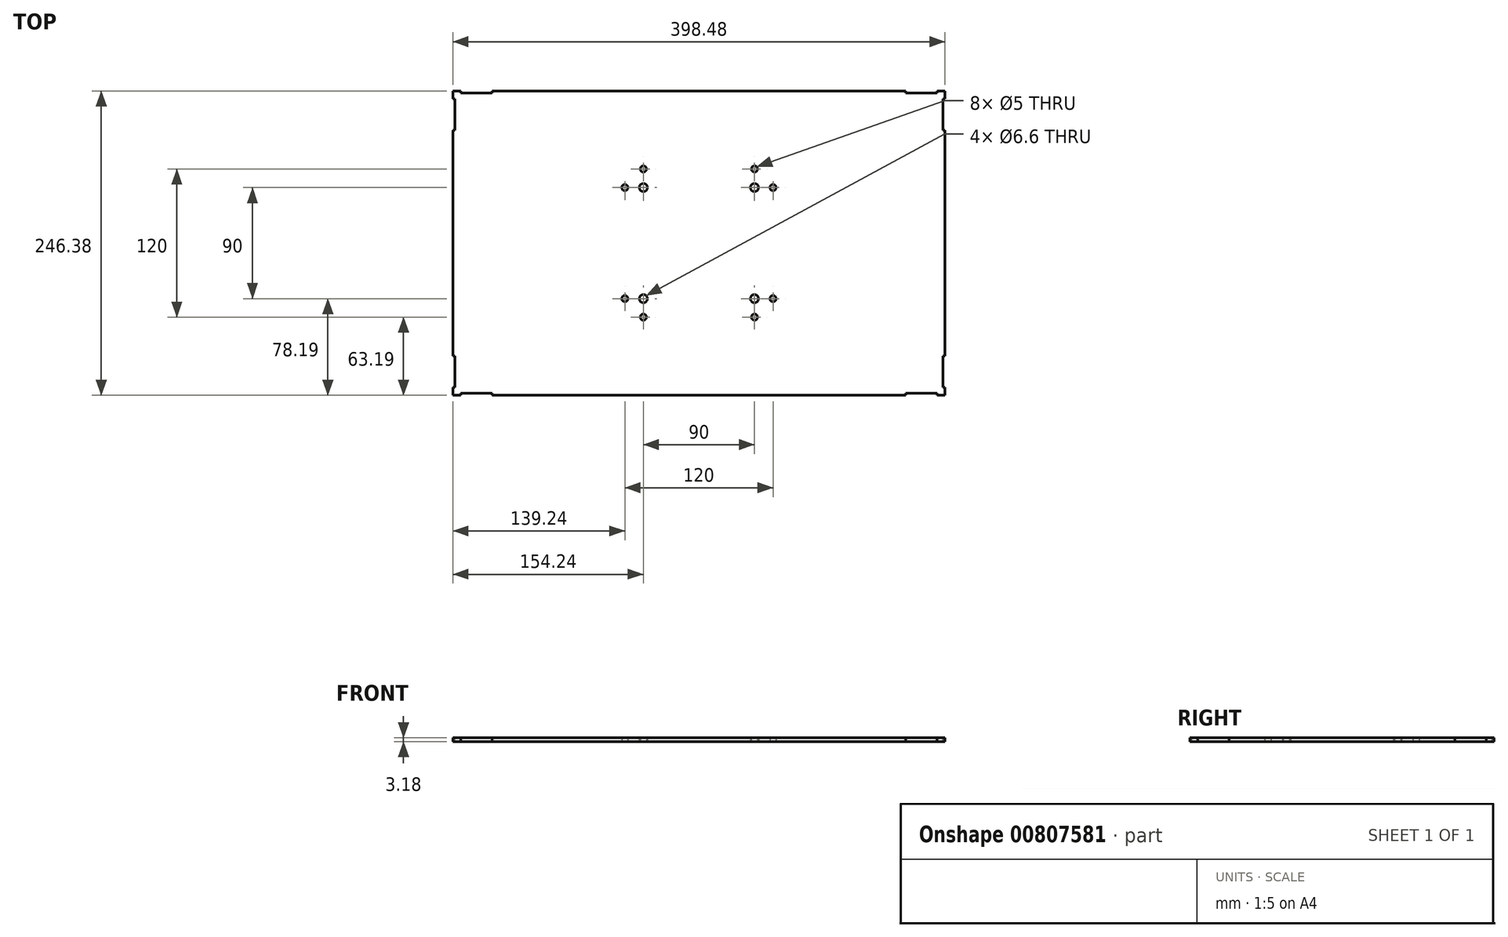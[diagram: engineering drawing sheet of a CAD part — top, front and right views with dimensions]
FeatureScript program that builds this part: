
annotation { "Feature Type Name" : "Feature", "Feature Type Description" : "" }
export const myFeature = defineFeature(function(context is Context, id is Id, definition is map)
    precondition{}
    {
        {
            var Q0;
            Q0=qCreatedBy(makeId("Top.planeOp"),FACE);
            var sketch = newSketch(context, id + "F0", { "sketchPlane" : qUnion([Q0])});
            skLineSegment(sketch, "E0.bottom", {"start": v(-199.24, 123.19) * mm, "end": v(199.24, 123.19) * mm});
            skLineSegment(sketch, "E0.top", {"start": v(-199.24, -123.2) * mm, "end": v(199.24, -123.2) * mm});
            skLineSegment(sketch, "E0.left", {"start": v(-199.24, 123.19) * mm, "end": v(-199.24, -123.2) * mm});
            skLineSegment(sketch, "E0.right", {"start": v(199.24, 123.19) * mm, "end": v(199.24, -123.19) * mm});
            skPoint(sketch, "E0.middle", {"position": v(0, 0) * mm});
            skLineSegment(sketch, "E1.bottom", {"start": v(45, 45) * mm, "end": v(-45, 45) * mm, "construction": true});
            skLineSegment(sketch, "E1.top", {"start": v(45, -45) * mm, "end": v(-45, -45) * mm, "construction": true});
            skLineSegment(sketch, "E1.left", {"start": v(45, 45) * mm, "end": v(45, -45) * mm, "construction": true});
            skLineSegment(sketch, "E1.right", {"start": v(-45, 45) * mm, "end": v(-45, -45) * mm, "construction": true});
            skCircle(sketch, "E2", {"center": v(-45, 45) * mm, "radius": 3.3 * mm});
            skCircle(sketch, "E3", {"center": v(45, 45) * mm, "radius": 3.3 * mm});
            skCircle(sketch, "E4", {"center": v(45, -45) * mm, "radius": 3.3 * mm});
            skCircle(sketch, "E5", {"center": v(-45, -45) * mm, "radius": 3.3 * mm});
            skCircle(sketch, "E6", {"center": v(-60, 45) * mm, "radius": 2.5 * mm});
            skCircle(sketch, "E7", {"center": v(-45, 60) * mm, "radius": 2.5 * mm});
            skCircle(sketch, "E8.MirrorC", {"center": v(45, 60) * mm, "radius": 2.5 * mm});
            skCircle(sketch, "E9.MirrorC", {"center": v(60, 45) * mm, "radius": 2.5 * mm});
            skCircle(sketch, "E10.MirrorC", {"center": v(45, -60) * mm, "radius": 2.5 * mm});
            skCircle(sketch, "E11.MirrorC", {"center": v(60, -45) * mm, "radius": 2.5 * mm});
            skCircle(sketch, "E12.MirrorC", {"center": v(-45, -60) * mm, "radius": 2.5 * mm});
            skCircle(sketch, "E13.MirrorC", {"center": v(-60, -45) * mm, "radius": 2.5 * mm});
            skSolve(sketch);
        }
        {
            var Q0;
            Q0=makeQuery(id+"F0.imprint","IMPRINT",FACE,{"disambiguationData":[TD([[makeQuery(id+"F0.imprint","IMPRINT",EDGE,{"derivedFrom":sQuery(id+"F0.wireOp",EDGE,"E0.bottom")}),-1.0]])]});
            extrude(context, id + "F1", {"entities" : qUnion([Q0]), "depth" : 3.17 * mm, "offsetDistance" : 25.4 * mm});
        }
        {
            var Q0;
            Q0=makeQuery(id+"F1.opExtrude","CAP_FACE",FACE,{"disambiguationData":[OSD([sQuery(id+"F0.wireOp",EDGE,"E0.bottom"),sQuery(id+"F0.wireOp",EDGE,"E0.top"),sQuery(id+"F0.wireOp",EDGE,"E0.left"),sQuery(id+"F0.wireOp",EDGE,"E0.right"),sQuery(id+"F0.wireOp",EDGE,"w9YSMrmx-gkuf-mAF0-RrVV-VzfJ2XjQqvrK.bottom"),sQuery(id+"F0.wireOp",EDGE,"w9YSMrmx-gkuf-mAF0-RrVV-VzfJ2XjQqvrK.top"),sQuery(id+"F0.wireOp",EDGE,"w9YSMrmx-gkuf-mAF0-RrVV-VzfJ2XjQqvrK.left"),sQuery(id+"F0.wireOp",EDGE,"w9YSMrmx-gkuf-mAF0-RrVV-VzfJ2XjQqvrK.right"),sQuery(id+"F0.wireOp",EDGE,"E2"),sQuery(id+"F0.wireOp",EDGE,"E3"),sQuery(id+"F0.wireOp",EDGE,"E4"),sQuery(id+"F0.wireOp",EDGE,"E5"),sQuery(id+"F0.wireOp",EDGE,"7fj2jC65-HHjj-RPa5-pwH1-fIjqxPNooKX1.bottom"),sQuery(id+"F0.wireOp",EDGE,"7fj2jC65-HHjj-RPa5-pwH1-fIjqxPNooKX1.top"),sQuery(id+"F0.wireOp",EDGE,"7fj2jC65-HHjj-RPa5-pwH1-fIjqxPNooKX1.right"),sQuery(id+"F0.wireOp",EDGE,"73IWlzh5-ptpZ-RGeC-0AsT-BQBUthGwBnOJ"),sQuery(id+"F0.wireOp",EDGE,"pzAkxvwE-vERC-Da5q-IG9L-KNYuP0dNzW4O"),sQuery(id+"F0.wireOp",EDGE,"hqBXGcnr-b5Qw-30Y7-EFE3-Enjm0PSFEsAV"),sQuery(id+"F0.wireOp",EDGE,"LVQ4rxL2-owo7-0TQt-NuUL-hCUhgpkdSAuj"),sQuery(id+"F0.wireOp",EDGE,"VEGctwco-K67i-BCNj-dZf2-I8q0qQZjCyYO"),sQuery(id+"F0.wireOp",EDGE,"W6IrgXfp-vklz-oZm7-d0sl-V1VckyniwT7Z")])],"isStart":false});
            var sketch = newSketch(context, id + "F2", { "sketchPlane" : qUnion([Q0])});
            skLineSegment(sketch, "E14.0", {"start": v(-199.24, 123.19) * mm, "end": v(199.24, 123.19) * mm, "construction": true});
            skLineSegment(sketch, "E14.1", {"start": v(-199.24, 123.19) * mm, "end": v(-199.24, -123.2) * mm, "construction": true});
            skLineSegment(sketch, "E14.2", {"start": v(-199.24, -123.2) * mm, "end": v(199.24, -123.2) * mm, "construction": true});
            skLineSegment(sketch, "E14.3", {"start": v(199.24, 123.19) * mm, "end": v(199.24, -123.2) * mm, "construction": true});
            skLineSegment(sketch, "E15.bottom", {"start": v(-192.89, 123.19) * mm, "end": v(-167.49, 123.19) * mm});
            skLineSegment(sketch, "E15.top", {"start": v(-192.89, 121.6) * mm, "end": v(-167.49, 121.6) * mm});
            skLineSegment(sketch, "E15.left", {"start": v(-192.89, 123.19) * mm, "end": v(-192.89, 121.6) * mm});
            skLineSegment(sketch, "E15.right", {"start": v(-167.49, 123.19) * mm, "end": v(-167.49, 121.6) * mm});
            skLineSegment(sketch, "E16.MirrorCS", {"start": v(192.89, 123.19) * mm, "end": v(192.89, 121.6) * mm});
            skLineSegment(sketch, "E17.MirrorCS", {"start": v(192.89, 121.6) * mm, "end": v(167.49, 121.6) * mm});
            skLineSegment(sketch, "E18.MirrorCS", {"start": v(167.49, 123.19) * mm, "end": v(167.49, 121.6) * mm});
            skLineSegment(sketch, "E19.MirrorCS", {"start": v(-192.89, -121.6) * mm, "end": v(-167.49, -121.6) * mm});
            skLineSegment(sketch, "E20.MirrorCS", {"start": v(-167.49, -123.19) * mm, "end": v(-167.49, -121.6) * mm});
            skLineSegment(sketch, "E21.MirrorCS", {"start": v(-192.89, -123.19) * mm, "end": v(-192.89, -121.6) * mm});
            skLineSegment(sketch, "E22.MirrorCS", {"start": v(167.49, -123.19) * mm, "end": v(167.49, -121.6) * mm});
            skLineSegment(sketch, "E23.MirrorCS", {"start": v(192.89, -121.6) * mm, "end": v(167.49, -121.6) * mm});
            skLineSegment(sketch, "E24.MirrorCS", {"start": v(192.89, -123.19) * mm, "end": v(192.89, -121.6) * mm});
            skLineSegment(sketch, "E25", {"start": v(167.49, 123.19) * mm, "end": v(192.89, 123.19) * mm});
            skLineSegment(sketch, "E26", {"start": v(-192.89, -123.2) * mm, "end": v(-167.49, -123.2) * mm});
            skLineSegment(sketch, "E27", {"start": v(167.49, -123.19) * mm, "end": v(192.89, -123.19) * mm});
            skLineSegment(sketch, "E28.bottom", {"start": v(-199.24, 116.84) * mm, "end": v(-197.65, 116.84) * mm});
            skLineSegment(sketch, "E28.top", {"start": v(-199.24, 91.44) * mm, "end": v(-197.65, 91.44) * mm});
            skLineSegment(sketch, "E28.left", {"start": v(-199.24, 116.84) * mm, "end": v(-199.24, 91.44) * mm});
            skLineSegment(sketch, "E28.right", {"start": v(-197.65, 116.84) * mm, "end": v(-197.65, 91.44) * mm});
            skLineSegment(sketch, "E29.MirrorCS", {"start": v(199.24, 116.84) * mm, "end": v(197.65, 116.84) * mm});
            skLineSegment(sketch, "E30.MirrorCS", {"start": v(199.24, 91.44) * mm, "end": v(197.65, 91.44) * mm});
            skLineSegment(sketch, "E31.MirrorCS", {"start": v(199.24, 116.84) * mm, "end": v(199.24, 91.44) * mm});
            skLineSegment(sketch, "E32.MirrorCS", {"start": v(197.65, 116.84) * mm, "end": v(197.65, 91.44) * mm});
            skLineSegment(sketch, "E33.MirrorCS", {"start": v(-199.24, -91.44) * mm, "end": v(-197.65, -91.44) * mm});
            skLineSegment(sketch, "E34.MirrorCS", {"start": v(-199.24, -116.84) * mm, "end": v(-197.65, -116.84) * mm});
            skLineSegment(sketch, "E35.MirrorCS", {"start": v(-199.24, -116.84) * mm, "end": v(-199.24, -91.44) * mm});
            skLineSegment(sketch, "E36.MirrorCS", {"start": v(-197.65, -116.84) * mm, "end": v(-197.65, -91.44) * mm});
            skLineSegment(sketch, "E37.MirrorCS", {"start": v(199.24, -116.84) * mm, "end": v(199.24, -91.44) * mm});
            skLineSegment(sketch, "E38.MirrorCS", {"start": v(197.65, -116.84) * mm, "end": v(197.65, -91.44) * mm});
            skLineSegment(sketch, "E39.MirrorCS", {"start": v(199.24, -116.84) * mm, "end": v(197.65, -116.84) * mm});
            skLineSegment(sketch, "E40.MirrorCS", {"start": v(199.24, -91.44) * mm, "end": v(197.65, -91.44) * mm});
            skLineSegment(sketch, "E41.MirrorCS", {"start": v(199.24, -123.19) * mm, "end": v(199.24, 123.2) * mm, "construction": true});
            skSolve(sketch);
        }
        {
            var Q0;
            Q0 = qSketchRegion(id + "F2", true);
            var Q1;
            Q1=makeQuery(id+"F1.opExtrude","CAP_FACE",FACE,{"disambiguationData":[OSD([sQuery(id+"F0.wireOp",EDGE,"E0.bottom"),sQuery(id+"F0.wireOp",EDGE,"E0.top"),sQuery(id+"F0.wireOp",EDGE,"E0.left"),sQuery(id+"F0.wireOp",EDGE,"E0.right"),sQuery(id+"F0.wireOp",EDGE,"w9YSMrmx-gkuf-mAF0-RrVV-VzfJ2XjQqvrK.bottom"),sQuery(id+"F0.wireOp",EDGE,"w9YSMrmx-gkuf-mAF0-RrVV-VzfJ2XjQqvrK.top"),sQuery(id+"F0.wireOp",EDGE,"w9YSMrmx-gkuf-mAF0-RrVV-VzfJ2XjQqvrK.left"),sQuery(id+"F0.wireOp",EDGE,"w9YSMrmx-gkuf-mAF0-RrVV-VzfJ2XjQqvrK.right"),sQuery(id+"F0.wireOp",EDGE,"E2"),sQuery(id+"F0.wireOp",EDGE,"E3"),sQuery(id+"F0.wireOp",EDGE,"E4"),sQuery(id+"F0.wireOp",EDGE,"E5"),sQuery(id+"F0.wireOp",EDGE,"7fj2jC65-HHjj-RPa5-pwH1-fIjqxPNooKX1.bottom"),sQuery(id+"F0.wireOp",EDGE,"7fj2jC65-HHjj-RPa5-pwH1-fIjqxPNooKX1.top"),sQuery(id+"F0.wireOp",EDGE,"7fj2jC65-HHjj-RPa5-pwH1-fIjqxPNooKX1.right"),sQuery(id+"F0.wireOp",EDGE,"73IWlzh5-ptpZ-RGeC-0AsT-BQBUthGwBnOJ"),sQuery(id+"F0.wireOp",EDGE,"pzAkxvwE-vERC-Da5q-IG9L-KNYuP0dNzW4O"),sQuery(id+"F0.wireOp",EDGE,"hqBXGcnr-b5Qw-30Y7-EFE3-Enjm0PSFEsAV"),sQuery(id+"F0.wireOp",EDGE,"LVQ4rxL2-owo7-0TQt-NuUL-hCUhgpkdSAuj"),sQuery(id+"F0.wireOp",EDGE,"VEGctwco-K67i-BCNj-dZf2-I8q0qQZjCyYO"),sQuery(id+"F0.wireOp",EDGE,"W6IrgXfp-vklz-oZm7-d0sl-V1VckyniwT7Z")])],"isStart":true});
            extrude(context, id + "F3", {"entities" : qUnion([Q0]), "operationType" : NewBodyOperationType.REMOVE, "endBound" : BoundingType.UP_TO_SURFACE, "oppositeDirection" : true, "depth" : 6.35 * mm, "endBoundEntityFace" : qUnion([Q1]), "offsetDistance" : 25 * mm});
        }
    });
